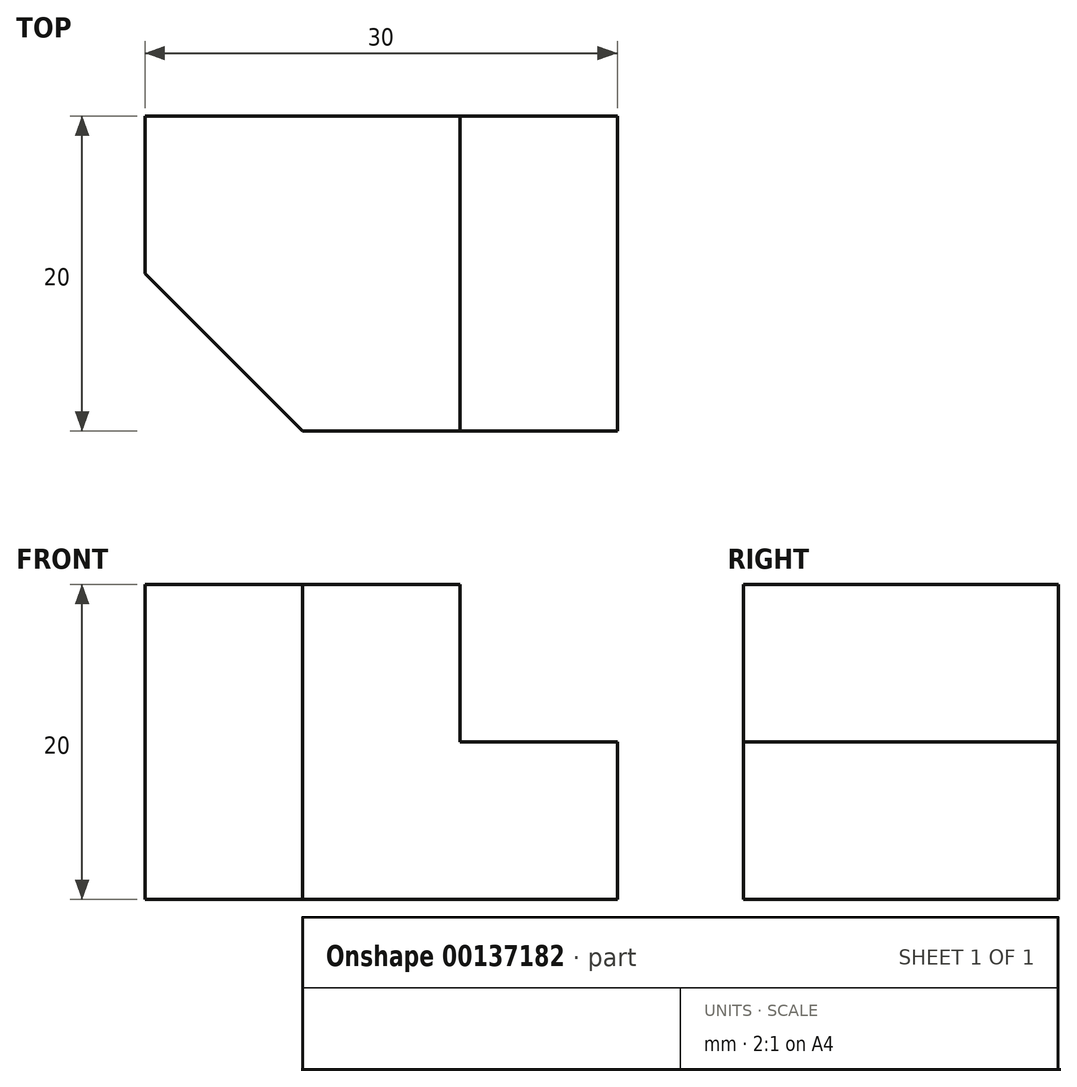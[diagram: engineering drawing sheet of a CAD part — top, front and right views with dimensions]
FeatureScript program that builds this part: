
annotation { "Feature Type Name" : "Feature", "Feature Type Description" : "" }
export const myFeature = defineFeature(function(context is Context, id is Id, definition is map)
    precondition{}
    {
        {
            var Q0;
            Q0=qCreatedBy(makeId("Front.planeOp"),FACE);
            var sketch = newSketch(context, id + "F0", { "sketchPlane" : qUnion([Q0])});
            skLineSegment(sketch, "E0.bottom", {"start": v(0, 0) * mm, "end": v(10, 0) * mm});
            skLineSegment(sketch, "E0.top", {"start": v(0, 20) * mm, "end": v(10, 20) * mm});
            skLineSegment(sketch, "E0.left", {"start": v(0, 0) * mm, "end": v(0, 20) * mm});
            skLineSegment(sketch, "E0.right", {"start": v(10, 0) * mm, "end": v(10, 20) * mm});
            skLineSegment(sketch, "E1.bottom", {"start": v(20, 10) * mm, "end": v(30, 10) * mm});
            skLineSegment(sketch, "E1.top", {"start": v(10, 0) * mm, "end": v(30, 0) * mm});
            skLineSegment(sketch, "E1.right", {"start": v(30, 10) * mm, "end": v(30, 0) * mm});
            skLineSegment(sketch, "E2", {"start": v(20, 10) * mm, "end": v(20, 20) * mm});
            skLineSegment(sketch, "E3", {"start": v(20, 20) * mm, "end": v(10, 20) * mm});
            skSolve(sketch);
        }
        {
            var Q0;
            Q0 = qSketchRegion(id + "F0", true);
            extrude(context, id + "F1", {"entities" : qUnion([Q0]), "depth" : 20 * mm});
        }
        {
            var Q0;
            Q0=makeQuery(id+"F1.opExtrude","SWEPT_FACE",FACE,{"disambiguationData":[OSD([sQuery(id+"F0.wireOp",EDGE,"E0.top"),sQuery(id+"F0.wireOp",EDGE,"E3")])]});
            var sketch = newSketch(context, id + "F2", { "sketchPlane" : qUnion([Q0])});
            skLineSegment(sketch, "E4", {"start": v(0, -10) * mm, "end": v(0, -20) * mm});
            skLineSegment(sketch, "E5", {"start": v(0, -20) * mm, "end": v(10, -20) * mm});
            skLineSegment(sketch, "E6", {"start": v(10, -20) * mm, "end": v(0, -10) * mm});
            skSolve(sketch);
        }
        {
            var Q0;
            Q0=makeQuery(id+"F2.imprint","IMPRINT",FACE,{"disambiguationData":[TD([[makeQuery(id+"F2.imprint","IMPRINT",EDGE,{"derivedFrom":sQuery(id+"F2.wireOp",EDGE,"E4")}),-1.0]])]});
            extrude(context, id + "F3", {"entities" : qUnion([Q0]), "operationType" : NewBodyOperationType.REMOVE, "endBound" : BoundingType.THROUGH_ALL, "oppositeDirection" : true, "depth" : 25 * mm});
        }
    });
